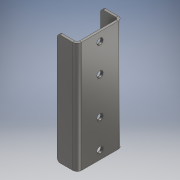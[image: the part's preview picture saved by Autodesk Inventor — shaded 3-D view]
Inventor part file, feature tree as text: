
AUTODESK INVENTOR PART (.ipt)
format: ipt  version: 2017 (Build 210142000, 142)  size: 143,360 bytes
history: native  units: mm
features: sheet_metal_op x3, sketch x2, fillet x1, hole x1, other x1, projected_geometry x1
ambient origin geometry x8: Origin, YZ Plane, XZ Plane, XY Plane, X Axis, Y Axis, Z Axis, Center Point
bodies: Solid1 (feature_tree)
feature tree (9):
  sheet_metal_op  "Contour Flange1"
  fillet  "Fillet1"  Radius=35.0mm
  hole  "Hole1"  [1 undecoded]
  sketch  "Sketch1"  dims[d1=35.0mm d2=80.0mm]
  other  "Plate1"
  sheet_metal_op  "Bend1"
  sheet_metal_op  "Corner1"
  sketch  "Sketch2"  dims[d3=4.0mm d4=2.0mm d5=8.0mm d6=3.9mm d8=3.9mm d9=0.5mm d10=16.0mm d11=4.0mm d12=3.9mm d13=5.0mm d14=15.0mm d15=50.0mm d16=50.0mm d17=15.0mm d18=11.0mm d19=6.0mm d20=3.023mm d21=2.0mm d22=14.3117mm d23=4.0mm d24=20.594885mm]
  projected_geometry  "Projected Loop1"
note: 1 required parameter value undecoded (feature->parameter linkage not recoverable at this tier; creation-order binding heuristic only, values carry confidence <= 0.55)
